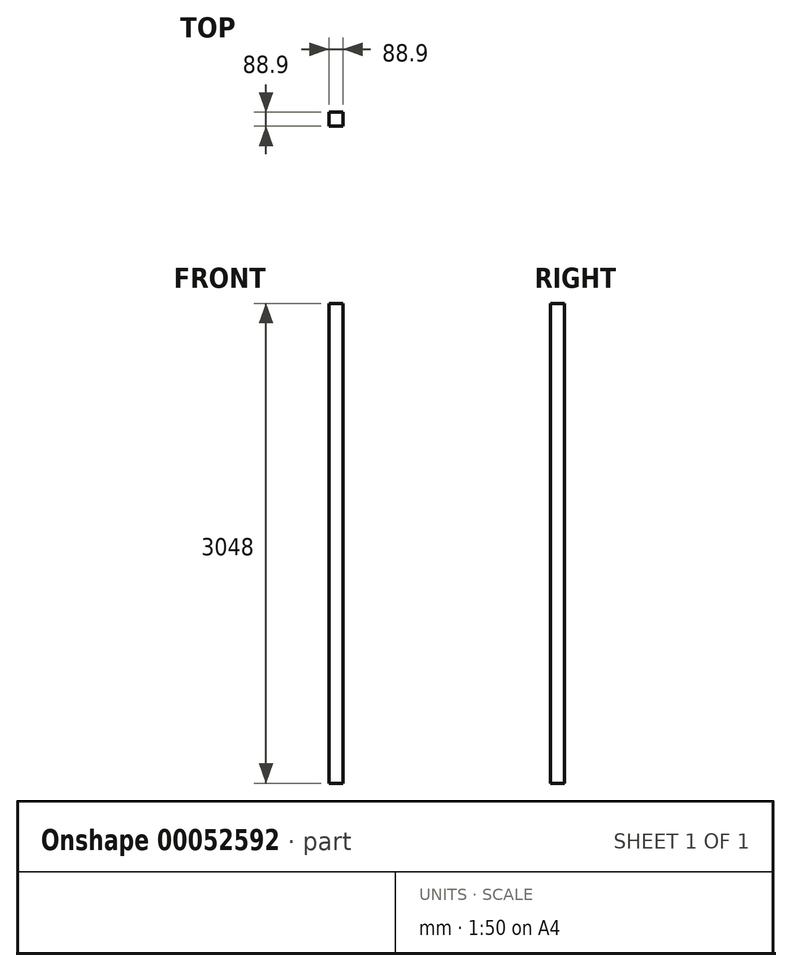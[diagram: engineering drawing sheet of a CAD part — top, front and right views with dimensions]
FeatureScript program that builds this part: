
annotation { "Feature Type Name" : "Feature", "Feature Type Description" : "" }
export const myFeature = defineFeature(function(context is Context, id is Id, definition is map)
    precondition{}
    {
        {
            var Q0;
            Q0=qCreatedBy(makeId("Top.planeOp"),FACE);
            var sketch = newSketch(context, id + "F1", { "sketchPlane" : qUnion([Q0])});
            skLineSegment(sketch, "E0.bottom", {"start": v(0, 0) * mm, "end": v(-88.9, 0) * mm});
            skLineSegment(sketch, "E0.top", {"start": v(0, 88.9) * mm, "end": v(-88.9, 88.9) * mm});
            skLineSegment(sketch, "E0.left", {"start": v(0, 0) * mm, "end": v(0, 88.9) * mm});
            skLineSegment(sketch, "E0.right", {"start": v(-88.9, 0) * mm, "end": v(-88.9, 88.9) * mm});
            skSolve(sketch);
        }
        {
            var Q0;
            Q0=makeQuery(id+"F1.imprint","IMPRINT",FACE,{"disambiguationData":[TD([[makeQuery(id+"F1.imprint","IMPRINT",EDGE,{"derivedFrom":sQuery(id+"F1.wireOp",EDGE,"E0.bottom")}),-1.0]])]});
            extrude(context, id + "F0", {"entities" : qUnion([Q0]), "depth" : 3048 * mm});
        }
    });
